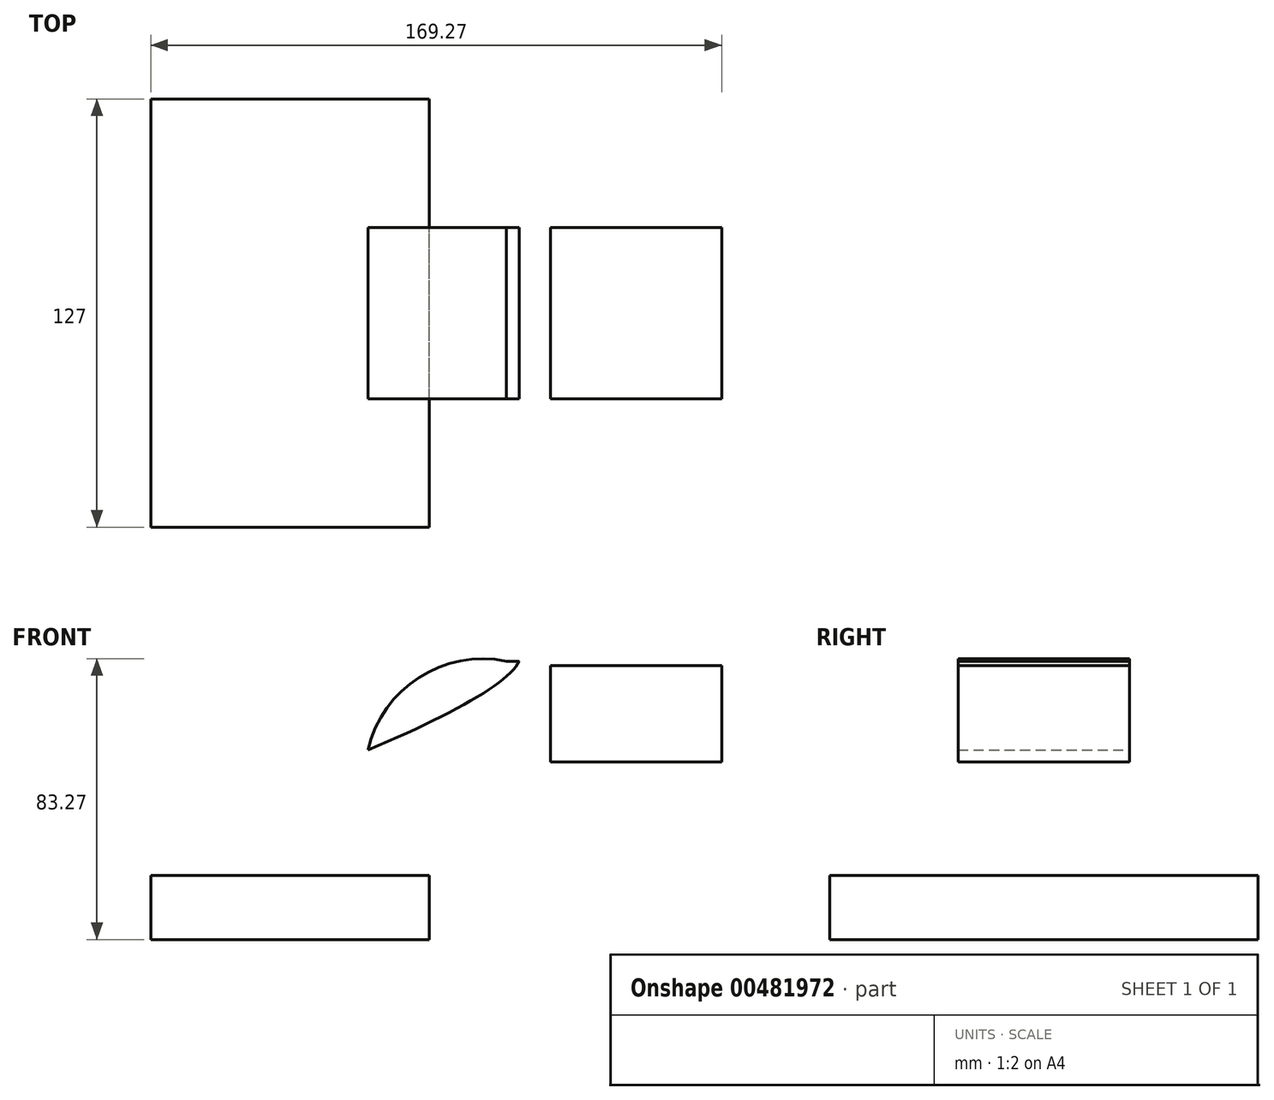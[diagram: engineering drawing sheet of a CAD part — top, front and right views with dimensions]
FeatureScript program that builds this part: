
annotation { "Feature Type Name" : "Feature", "Feature Type Description" : "" }
export const myFeature = defineFeature(function(context is Context, id is Id, definition is map)
    precondition{}
    {
        {
            var Q0;
            Q0=qCreatedBy(makeId("Front.planeOp"),FACE);
            var sketch = newSketch(context, id + "F0", { "sketchPlane" : qUnion([Q0])});
            skLineSegment(sketch, "E0.bottom", {"start": v(41.28, -9.52) * mm, "end": v(-41.28, -9.53) * mm});
            skLineSegment(sketch, "E0.top", {"start": v(41.28, 9.53) * mm, "end": v(-41.28, 9.53) * mm});
            skLineSegment(sketch, "E0.left", {"start": v(41.28, -9.52) * mm, "end": v(41.28, 9.53) * mm});
            skLineSegment(sketch, "E0.right", {"start": v(-41.28, -9.52) * mm, "end": v(-41.28, 9.53) * mm});
            skPoint(sketch, "E0.middle", {"position": v(0, 0) * mm});
            skLineSegment(sketch, "E1.bottom", {"start": v(128, 43.18) * mm, "end": v(77.2, 43.18) * mm});
            skLineSegment(sketch, "E1.top", {"start": v(128, 71.76) * mm, "end": v(77.2, 71.76) * mm});
            skLineSegment(sketch, "E1.left", {"start": v(128, 43.18) * mm, "end": v(128, 71.76) * mm});
            skLineSegment(sketch, "E1.right", {"start": v(77.2, 43.18) * mm, "end": v(77.2, 71.76) * mm});
            skPoint(sketch, "E1.middle", {"position": v(102.6, 57.47) * mm});
            skLineSegment(sketch, "E2", {"start": v(41.28, 9.53) * mm, "end": v(41.28, 38.81) * mm});
            skArc(sketch, "E3", {"start": v(41.27, 38.81) * mm, "mid": v(47.73, 51.6) * mm, "end": v(61.85, 53.98) * mm});
            skLineSegment(sketch, "E4", {"start": v(61.85, 53.98) * mm, "end": v(105.7, 53.98) * mm});
            skLineSegment(sketch, "E5.0", {"start": v(22.22, 9.53) * mm, "end": v(22.22, 38.81) * mm});
            skArc(sketch, "E6.0", {"start": v(22.23, 38.81) * mm, "mid": v(36.43, 66.93) * mm, "end": v(67.5, 72.17) * mm});
            skLineSegment(sketch, "E7.0", {"start": v(61.85, 73.03) * mm, "end": v(105.7, 73.03) * mm});
            skFitSpline(sketch, "E8", {"points": [v(-116.56, 9.97) * mm, v(67.5, 72.17) * mm, v(-56.25, 61.73) * mm, v(-116.56, 9.97) * mm]});
            skSolve(sketch);
        }
        {
            var Q0;
            Q0=makeQuery(id+"F0.imprint","IMPRINT",FACE,{"disambiguationData":[TD([[makeQuery(id+"F0.imprint","IMPRINT",EDGE,{"derivedFrom":sQuery(id+"F0.wireOp",EDGE,"E0.bottom")}),-1.0]])]});
            extrude(context, id + "F1", {"entities" : qUnion([Q0]), "endBound" : BoundingType.SYMMETRIC, "depth" : 127 * mm});
        }
        {
            var Q0;
            {var subQ0=sQuery(id+"F0.wireOp",EDGE,"E8");var subQ1=sQuery(id+"F0.wireOp",EDGE,"E6.0");var subQ2=makeQuery(id+"F0.imprint","INTERSECT",VERTEX,{"disambiguationData":[OD(1.0)],"derivedFrom":[subQ1,subQ0]});Q0=makeQuery(id+"F0.imprint","IMPRINT",FACE,{"disambiguationData":[TD([[makeQuery(id+"F0.imprint","IMPRINT",EDGE,{"disambiguationData":[TD([[subQ2,-1.0]])],"derivedFrom":subQ1}),1.0]])]});}
            extrude(context, id + "F2", {"entities" : qUnion([Q0]), "endBound" : BoundingType.SYMMETRIC, "depth" : 50.8 * mm});
        }
        {
            var Q0;
            {var subQ1=sQuery(id+"F0.wireOp",EDGE,"E1.bottom");Q0=makeQuery(id+"F0.imprint","IMPRINT",FACE,{"disambiguationData":[TD([[makeQuery(id+"F0.imprint","IMPRINT",EDGE,{"derivedFrom":subQ1}),-1.0]])]});}
            var Q1;
            {var subQ0=sQuery(id+"F0.wireOp",EDGE,"E8");var subQ1=sQuery(id+"F0.wireOp",EDGE,"E6.0");var subQ2=makeQuery(id+"F0.imprint","INTERSECT",VERTEX,{"disambiguationData":[OD(1.0)],"derivedFrom":[subQ1,subQ0]});Q1=makeQuery(id+"F0.imprint","IMPRINT",FACE,{"disambiguationData":[TD([[makeQuery(id+"F0.imprint","IMPRINT",EDGE,{"disambiguationData":[TD([[subQ2,-1.0]])],"derivedFrom":subQ1}),-1.0]])]});}
            extrude(context, id + "F3", {"entities" : qUnion([Q0, Q1]), "operationType" : NewBodyOperationType.ADD, "endBound" : BoundingType.SYMMETRIC, "depth" : 50.8 * mm});
        }
    });
